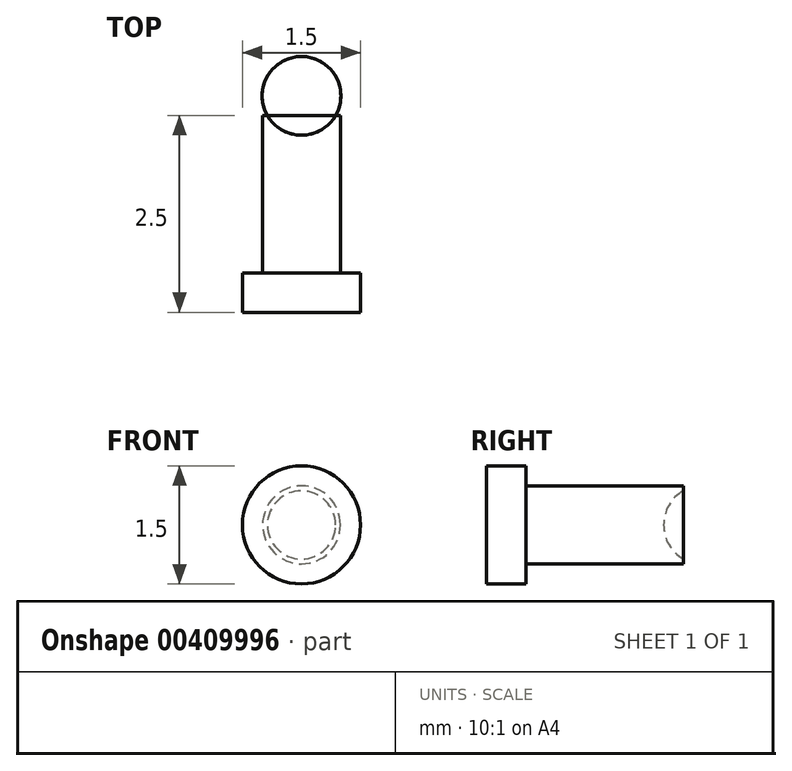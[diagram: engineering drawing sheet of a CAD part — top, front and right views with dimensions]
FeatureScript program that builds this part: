
annotation { "Feature Type Name" : "Feature", "Feature Type Description" : "" }
export const myFeature = defineFeature(function(context is Context, id is Id, definition is map)
    precondition{}
    {
        {
            var Q0;
            Q0=qCreatedBy(makeId("Front.planeOp"),FACE);
            var sketch = newSketch(context, id + "F0", { "sketchPlane" : qUnion([Q0])});
            skCircle(sketch, "E0", {"center": v(0, 0) * mm, "radius": 0.5 * mm});
            skSolve(sketch);
        }
        {
            var Q0;
            Q0=makeQuery(id+"F0.imprint","IMPRINT",FACE,{"disambiguationData":[TD([[makeQuery(id+"F0.imprint","IMPRINT",EDGE,{"derivedFrom":sQuery(id+"F0.wireOp",EDGE,"E0")}),1.0]])]});
            extrude(context, id + "F1", {"entities" : qUnion([Q0]), "depth" : 2 * mm});
        }
        {
            var Q0;
            Q0=makeQuery(id+"F1.opExtrude","CAP_FACE",FACE,{"disambiguationData":[OSD([sQuery(id+"F0.wireOp",EDGE,"E0")])],"isStart":false});
            var sketch = newSketch(context, id + "F2", { "sketchPlane" : qUnion([Q0])});
            skCircle(sketch, "E1", {"center": v(0, 0) * mm, "radius": 0.75 * mm});
            skSolve(sketch);
        }
        {
            var Q0;
            Q0=makeQuery(id+"F2.imprint","IMPRINT",FACE,{"disambiguationData":[TD([[makeQuery(id+"F2.imprint","IMPRINT",EDGE,{"derivedFrom":sQuery(id+"F2.wireOp",EDGE,"E1")}),1.0]])]});
            var Q1;
            Q1=makeQuery(id+"F2.imprint","IMPRINT",FACE,{"disambiguationData":[TD([[makeQuery(id+"F2.imprint","IMPRINT",EDGE,{"derivedFrom":makeQuery(id+"F1.opExtrude","CAP_EDGE",EDGE,{"disambiguationData":[OSD([sQuery(id+"F0.wireOp",EDGE,"E0")])],"isStart":false})}),1.0]])]});
            extrude(context, id + "F3", {"entities" : qUnion([Q0, Q1]), "operationType" : NewBodyOperationType.ADD, "depth" : 0.5 * mm});
        }
        {
            var Q0;
            Q0=qCreatedBy(makeId("Right.planeOp"),FACE);
            var sketch = newSketch(context, id + "F4", { "sketchPlane" : qUnion([Q0])});
            skArc(sketch, "E2", {"start": v(0.25, 0.5) * mm, "mid": v(-0.25, 0) * mm, "end": v(0.25, -0.5) * mm});
            skLineSegment(sketch, "E3", {"start": v(0.25, 0) * mm, "end": v(0.25, 0.5) * mm});
            skLineSegment(sketch, "E4", {"start": v(0.25, 0) * mm, "end": v(0.25, -0.5) * mm});
            skSolve(sketch);
        }
        {
            var Q0;
            Q0=makeQuery(id+"F4.imprint","IMPRINT",FACE,{"disambiguationData":[TD([[makeQuery(id+"F4.imprint","IMPRINT",EDGE,{"derivedFrom":sQuery(id+"F4.wireOp",EDGE,"E2")}),1.0]])]});
            var Q1;
            Q1=sQuery(id+"F4.wireOp",EDGE,"E3");
            revolve(context, id + "F5", {"operationType" : NewBodyOperationType.REMOVE, "entities" : qUnion([Q0]), "axis" : qUnion([Q1]), "revolveType" : RevolveType.FULL, "oppositeDirection" : true});
        }
    });
